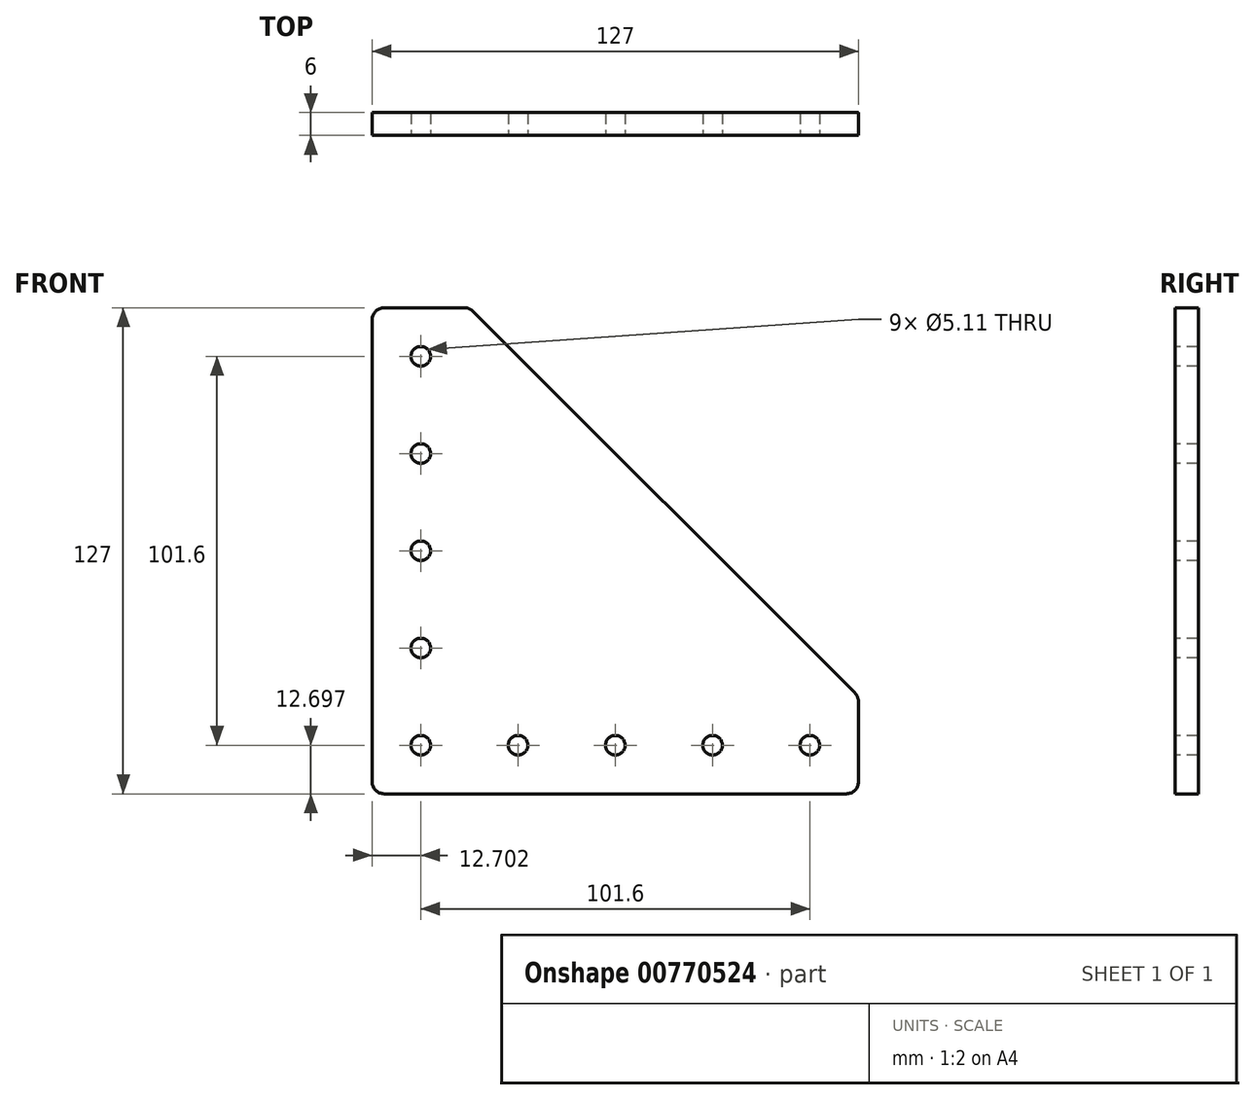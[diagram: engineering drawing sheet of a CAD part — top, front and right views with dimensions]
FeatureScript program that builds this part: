
annotation { "Feature Type Name" : "Feature", "Feature Type Description" : "" }
export const myFeature = defineFeature(function(context is Context, id is Id, definition is map)
    precondition{}
    {
        {
            var Q0;
            Q0=qCreatedBy(makeId("Front.planeOp"),FACE);
            var sketch = newSketch(context, id + "F0", { "sketchPlane" : qUnion([Q0])});
            skLineSegment(sketch, "E0", {"start": v(-148.33, 136.82) * mm, "end": v(-148.33, 16.17) * mm});
            skLineSegment(sketch, "E1", {"start": v(-145.15, 13) * mm, "end": v(-24.5, 13) * mm});
            skLineSegment(sketch, "E2", {"start": v(-21.33, 16.17) * mm, "end": v(-21.33, 37.08) * mm});
            skLineSegment(sketch, "E3", {"start": v(-22.26, 39.33) * mm, "end": v(-122, 139.07) * mm});
            skLineSegment(sketch, "E4", {"start": v(-124.24, 140) * mm, "end": v(-145.15, 140) * mm});
            skPoint(sketch, "E5.visualSharp", {"position": v(-148.33, 140) * mm});
            skArc(sketch, "E5.filletArc", {"start": v(-145.15, 140) * mm, "mid": v(-147.4, 139.07) * mm, "end": v(-148.33, 136.82) * mm});
            skPoint(sketch, "E6.visualSharp", {"position": v(-148.33, 13) * mm});
            skArc(sketch, "E6.filletArc", {"start": v(-148.33, 16.17) * mm, "mid": v(-147.4, 13.93) * mm, "end": v(-145.15, 13) * mm});
            skPoint(sketch, "E7.visualSharp", {"position": v(-21.33, 13) * mm});
            skArc(sketch, "E7.filletArc", {"start": v(-24.5, 13) * mm, "mid": v(-22.26, 13.93) * mm, "end": v(-21.33, 16.17) * mm});
            skPoint(sketch, "E8.visualSharp", {"position": v(-21.33, 38.4) * mm});
            skArc(sketch, "E8.filletArc", {"start": v(-21.33, 37.08) * mm, "mid": v(-21.57, 38.3) * mm, "end": v(-22.26, 39.33) * mm});
            skPoint(sketch, "E9.visualSharp", {"position": v(-122.93, 140) * mm});
            skArc(sketch, "E9.filletArc", {"start": v(-122, 139.07) * mm, "mid": v(-123.03, 139.76) * mm, "end": v(-124.24, 140) * mm});
            skSolve(sketch);
        }
        {
            var Q0;
            Q0=makeQuery(id+"F0.imprint","IMPRINT",FACE,{"disambiguationData":[TD([[makeQuery(id+"F0.imprint","IMPRINT",EDGE,{"derivedFrom":sQuery(id+"F0.wireOp",EDGE,"E0")}),1.0]])]});
            extrude(context, id + "F1", {"entities" : qUnion([Q0]), "depth" : 6 * mm, "offsetDistance" : 25.4 * mm});
        }
        {
            var Q0;
            Q0=makeQuery(id+"F1.opExtrude","CAP_FACE",FACE,{"disambiguationData":[OSD([sQuery(id+"F0.wireOp",EDGE,"E0"),sQuery(id+"F0.wireOp",EDGE,"E1"),sQuery(id+"F0.wireOp",EDGE,"E2"),sQuery(id+"F0.wireOp",EDGE,"E3"),sQuery(id+"F0.wireOp",EDGE,"E4")])],"isStart":false});
            var sketch = newSketch(context, id + "F2", { "sketchPlane" : qUnion([Q0])});
            skCircle(sketch, "E10", {"center": v(-135.63, 127.3) * mm, "radius": 2.55 * mm});
            skCircle(sketch, "E11.0.1.0", {"center": v(-135.63, 101.9) * mm, "radius": 2.55 * mm});
            skCircle(sketch, "E11.0.2.0", {"center": v(-135.63, 76.5) * mm, "radius": 2.55 * mm});
            skCircle(sketch, "E11.0.3.0", {"center": v(-135.63, 51.1) * mm, "radius": 2.55 * mm});
            skCircle(sketch, "E11.0.4.0", {"center": v(-135.63, 25.7) * mm, "radius": 2.55 * mm});
            skLineSegment(sketch, "E11.direction1", {"start": v(-135.63, 127.3) * mm, "end": v(-110.23, 127.3) * mm, "construction": true});
            skLineSegment(sketch, "E11.direction2", {"start": v(-135.63, 127.3) * mm, "end": v(-135.63, 101.9) * mm, "construction": true});
            skCircle(sketch, "E12.1.0.0", {"center": v(-110.23, 25.7) * mm, "radius": 2.55 * mm});
            skCircle(sketch, "E12.2.0.0", {"center": v(-84.83, 25.7) * mm, "radius": 2.55 * mm});
            skCircle(sketch, "E12.3.0.0", {"center": v(-59.43, 25.7) * mm, "radius": 2.55 * mm});
            skCircle(sketch, "E12.4.0.0", {"center": v(-34.03, 25.7) * mm, "radius": 2.55 * mm});
            skLineSegment(sketch, "E12.direction1", {"start": v(-135.63, 25.7) * mm, "end": v(-110.23, 25.7) * mm, "construction": true});
            skSolve(sketch);
        }
        {
            var Q0;
            Q0=sQuery(id+"F2.wireOp",VERTEX,"E11.0.2.0.center");
            var Q1;
            Q1=sQuery(id+"F2.wireOp",VERTEX,"E11.0.3.0.center");
            var Q2;
            Q2=sQuery(id+"F2.wireOp",VERTEX,"E11.0.4.0.center");
            var Q3;
            Q3=sQuery(id+"F2.wireOp",VERTEX,"E11.0.1.0.center");
            var Q4;
            Q4=sQuery(id+"F2.wireOp",VERTEX,"E11.direction1.start");
            var Q5;
            Q5=sQuery(id+"F2.wireOp",VERTEX,"E12.1.0.0.center");
            var Q6;
            Q6=sQuery(id+"F2.wireOp",VERTEX,"E12.2.0.0.center");
            var Q7;
            Q7=sQuery(id+"F2.wireOp",VERTEX,"E12.3.0.0.center");
            var Q8;
            Q8=sQuery(id+"F2.wireOp",VERTEX,"E12.4.0.0.center");
            var Q9;
            Q9=makeQuery(id+"F1.opExtrude","SWEPT_BODY",BODY,{"disambiguationData":[OSD([sQuery(id+"F0.wireOp",EDGE,"E0"),sQuery(id+"F0.wireOp",EDGE,"E1"),sQuery(id+"F0.wireOp",EDGE,"E2"),sQuery(id+"F0.wireOp",EDGE,"E3"),sQuery(id+"F0.wireOp",EDGE,"E4")])]});
            hole(context, id + "F3", {"style" : HoleStyle.SIMPLE, "endStyle" : HoleEndStyle.BLIND, "holeDiameter" : 5.1 * mm, "majorDiameter" : 6.35 * mm, "holeDepth" : 50.8 * mm, "isTappedThrough" : true, "tappedDepth" : 12.7 * mm, "tapClearance" : 3, "startFromSketch" : true, "locations" : qUnion([Q0, Q1, Q2, Q3, Q4, Q5, Q6, Q7, Q8]), "scope" : qUnion([Q9])});
        }
    });
